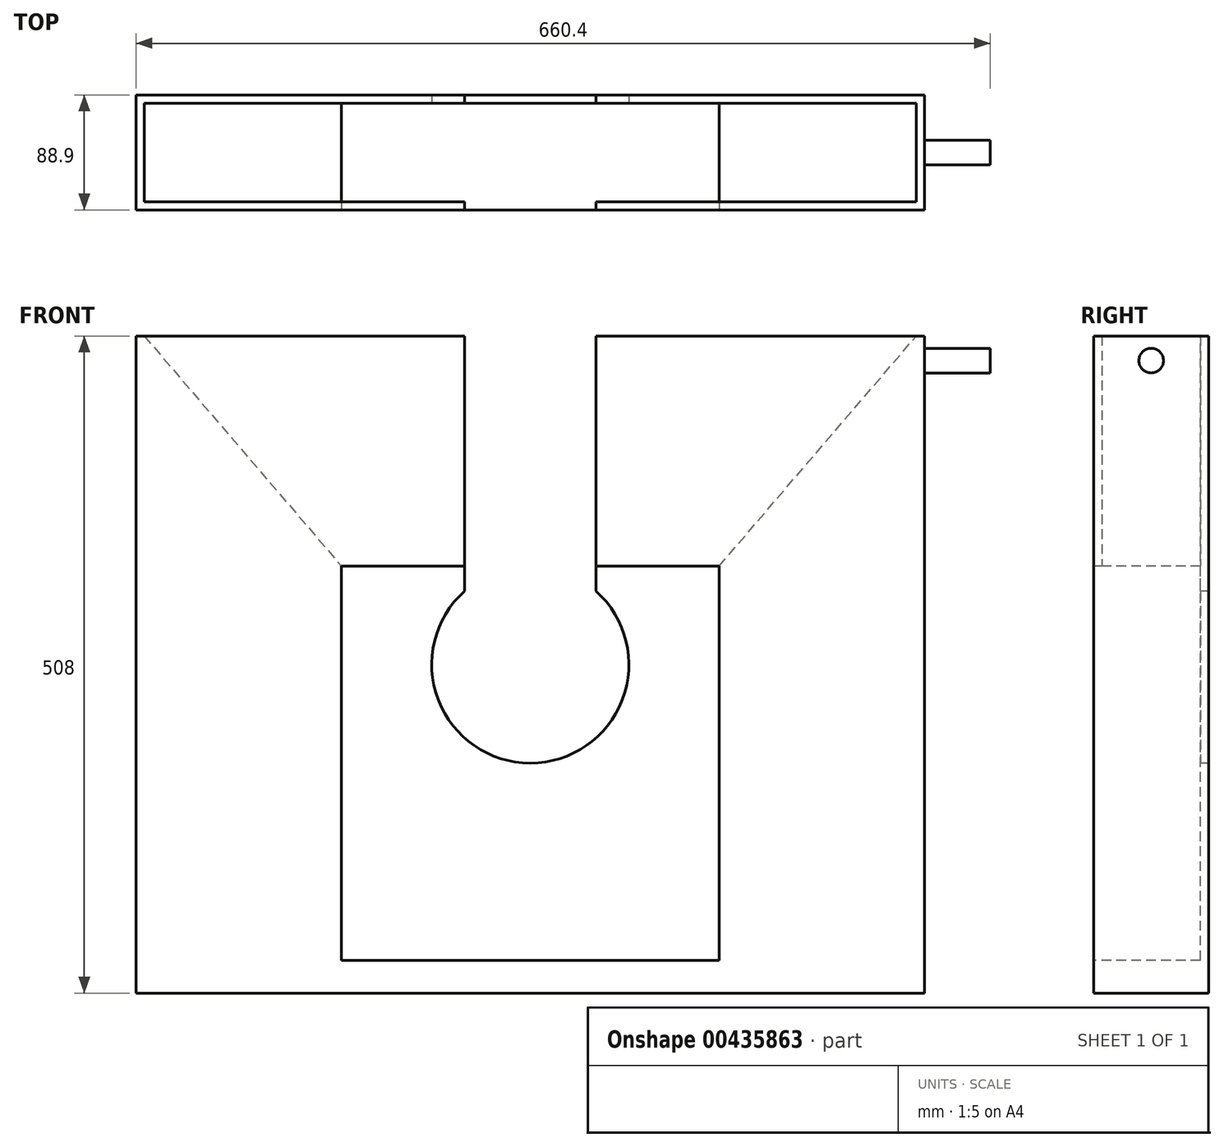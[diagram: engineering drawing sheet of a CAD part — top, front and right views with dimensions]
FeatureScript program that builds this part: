
annotation { "Feature Type Name" : "Feature", "Feature Type Description" : "" }
export const myFeature = defineFeature(function(context is Context, id is Id, definition is map)
    precondition{}
    {
        {
            var Q0;
            Q0=qCreatedBy(makeId("Front.planeOp"),FACE);
            var sketch = newSketch(context, id + "F0", { "sketchPlane" : qUnion([Q0])});
            skLineSegment(sketch, "E0.bottom", {"start": v(-304.8, 254) * mm, "end": v(304.8, 254) * mm});
            skLineSegment(sketch, "E0.top", {"start": v(-304.8, -254) * mm, "end": v(304.8, -254) * mm});
            skLineSegment(sketch, "E0.left", {"start": v(-304.8, 254) * mm, "end": v(-304.8, -254) * mm});
            skLineSegment(sketch, "E0.right", {"start": v(304.8, 254) * mm, "end": v(304.8, -254) * mm});
            skPoint(sketch, "E0.middle", {"position": v(0, 0) * mm});
            skSolve(sketch);
        }
        {
            var Q0;
            Q0=makeQuery(id+"F0.imprint","IMPRINT",FACE,{"disambiguationData":[TD([[makeQuery(id+"F0.imprint","IMPRINT",EDGE,{"derivedFrom":sQuery(id+"F0.wireOp",EDGE,"E0.bottom")}),-1.0]])]});
            extrude(context, id + "F1", {"entities" : qUnion([Q0]), "depth" : 88.9 * mm});
        }
        {
            var Q0;
            Q0=makeQuery(id+"F1.opExtrude","SWEPT_FACE",FACE,{"disambiguationData":[OSD([sQuery(id+"F0.wireOp",EDGE,"E0.bottom")])]});
            var sketch = newSketch(context, id + "F2", { "sketchPlane" : qUnion([Q0])});
            skLineSegment(sketch, "E1.bottom", {"start": v(-298.45, -6.35) * mm, "end": v(298.45, -6.35) * mm});
            skLineSegment(sketch, "E1.top", {"start": v(-298.45, -88.9) * mm, "end": v(298.45, -88.9) * mm});
            skLineSegment(sketch, "E1.left", {"start": v(-298.45, -6.35) * mm, "end": v(-298.45, -88.9) * mm});
            skLineSegment(sketch, "E1.right", {"start": v(298.45, -6.35) * mm, "end": v(298.45, -88.9) * mm});
            skSolve(sketch);
        }
        {
            var Q0;
            Q0=makeQuery(id+"F2.imprint","IMPRINT",FACE,{"disambiguationData":[TD([[makeQuery(id+"F2.imprint","IMPRINT",EDGE,{"derivedFrom":sQuery(id+"F2.wireOp",EDGE,"E1.bottom")}),-1.0]])]});
            extrude(context, id + "F3", {"entities" : qUnion([Q0]), "operationType" : NewBodyOperationType.REMOVE, "oppositeDirection" : true, "depth" : 482.6 * mm});
        }
        {
            var Q0;
            Q0=makeQuery(id+"F1.opExtrude","SWEPT_FACE",FACE,{"disambiguationData":[OSD([sQuery(id+"F0.wireOp",EDGE,"E0.right")])]});
            var sketch = newSketch(context, id + "F4", { "sketchPlane" : qUnion([Q0])});
            skCircle(sketch, "E2", {"center": v(-44.45, 234.95) * mm, "radius": 9.53 * mm});
            skSolve(sketch);
        }
        {
            var Q0;
            Q0=makeQuery(id+"F4.imprint","IMPRINT",FACE,{"disambiguationData":[TD([[makeQuery(id+"F4.imprint","IMPRINT",EDGE,{"derivedFrom":sQuery(id+"F4.wireOp",EDGE,"E2")}),1.0]])]});
            extrude(context, id + "F5", {"entities" : qUnion([Q0]), "operationType" : NewBodyOperationType.ADD, "depth" : 50.8 * mm});
        }
        {
            var Q0;
            Q0=makeQuery(id+"F1.opExtrude","CAP_FACE",FACE,{"disambiguationData":[OSD([sQuery(id+"F0.wireOp",EDGE,"E0.bottom"),sQuery(id+"F0.wireOp",EDGE,"E0.top"),sQuery(id+"F0.wireOp",EDGE,"E0.left"),sQuery(id+"F0.wireOp",EDGE,"E0.right")])],"isStart":false});
            var sketch = newSketch(context, id + "F6", { "sketchPlane" : qUnion([Q0])});
            skLineSegment(sketch, "E3", {"start": v(-298.45, -228.6) * mm, "end": v(-298.45, 76.2) * mm});
            skLineSegment(sketch, "E4", {"start": v(-298.45, 76.2) * mm, "end": v(-146.05, 76.2) * mm});
            skLineSegment(sketch, "E5", {"start": v(-146.05, 76.2) * mm, "end": v(146.05, 76.2) * mm});
            skLineSegment(sketch, "E6", {"start": v(146.05, 76.2) * mm, "end": v(298.45, 76.2) * mm});
            skLineSegment(sketch, "E7", {"start": v(-146.05, 76.2) * mm, "end": v(-298.45, 254) * mm});
            skLineSegment(sketch, "E8", {"start": v(-298.45, 254) * mm, "end": v(-298.45, 76.2) * mm});
            skLineSegment(sketch, "E9", {"start": v(146.05, 76.2) * mm, "end": v(298.45, 254) * mm});
            skLineSegment(sketch, "E10", {"start": v(298.45, 254) * mm, "end": v(298.45, 76.2) * mm});
            skSolve(sketch);
        }
        {
            var Q0;
            Q0=makeQuery(id+"F6.imprint","IMPRINT",FACE,{"disambiguationData":[TD([[makeQuery(id+"F6.imprint","IMPRINT",EDGE,{"derivedFrom":sQuery(id+"F6.wireOp",EDGE,"E4")}),1.0]])]});
            var Q1;
            Q1=makeQuery(id+"F6.imprint","IMPRINT",FACE,{"disambiguationData":[TD([[makeQuery(id+"F6.imprint","IMPRINT",EDGE,{"derivedFrom":sQuery(id+"F6.wireOp",EDGE,"E6")}),1.0]])]});
            var Q2;
            Q2=makeQuery(id+"F3.boolean.opBoolean","COPY",FACE,{"derivedFrom":makeQuery(id+"F3.opExtrude","SWEPT_FACE",FACE,{"disambiguationData":[OSD([sQuery(id+"F2.wireOp",EDGE,"E1.bottom")])]})});
            extrude(context, id + "F7", {"entities" : qUnion([Q0, Q1]), "operationType" : NewBodyOperationType.ADD, "endBound" : BoundingType.UP_TO_SURFACE, "oppositeDirection" : true, "endBoundEntityFace" : qUnion([Q2]), "depth" : 25.4 * mm});
        }
        {
            var Q0;
            Q0=makeQuery(id+"F7.boolean.opBoolean","MERGE",FACE,{"derivedFrom":[makeQuery(id+"F1.opExtrude","CAP_FACE",FACE,{"disambiguationData":[OSD([sQuery(id+"F0.wireOp",EDGE,"E0.bottom"),sQuery(id+"F0.wireOp",EDGE,"E0.top"),sQuery(id+"F0.wireOp",EDGE,"E0.left"),sQuery(id+"F0.wireOp",EDGE,"E0.right")])],"isStart":false}),makeQuery(id+"F7.opExtrude","CAP_FACE",FACE,{"disambiguationData":[OSD([sQuery(id+"F6.wireOp",EDGE,"E4"),sQuery(id+"F6.wireOp",EDGE,"E7"),sQuery(id+"F6.wireOp",EDGE,"E8")])],"isStart":true}),makeQuery(id+"F7.opExtrude","CAP_FACE",FACE,{"disambiguationData":[OSD([sQuery(id+"F6.wireOp",EDGE,"E6"),sQuery(id+"F6.wireOp",EDGE,"E9"),sQuery(id+"F6.wireOp",EDGE,"E10")])],"isStart":true})]});
            var sketch = newSketch(context, id + "F8", { "sketchPlane" : qUnion([Q0])});
            skLineSegment(sketch, "E11.bottom", {"start": v(-146.05, 76.2) * mm, "end": v(-298.45, 76.2) * mm});
            skLineSegment(sketch, "E11.top", {"start": v(-146.05, -228.6) * mm, "end": v(-298.45, -228.6) * mm});
            skLineSegment(sketch, "E11.left", {"start": v(-146.05, 76.2) * mm, "end": v(-146.05, -228.6) * mm});
            skLineSegment(sketch, "E11.right", {"start": v(-298.45, 76.2) * mm, "end": v(-298.45, -228.6) * mm});
            skLineSegment(sketch, "E12.bottom", {"start": v(146.05, 76.2) * mm, "end": v(298.45, 76.2) * mm});
            skLineSegment(sketch, "E12.top", {"start": v(146.05, -228.6) * mm, "end": v(298.45, -228.6) * mm});
            skLineSegment(sketch, "E12.left", {"start": v(146.05, 76.2) * mm, "end": v(146.05, -228.6) * mm});
            skLineSegment(sketch, "E12.right", {"start": v(298.45, 76.2) * mm, "end": v(298.45, -228.6) * mm});
            skSolve(sketch);
        }
        {
            var Q0;
            Q0=makeQuery(id+"F8.imprint","IMPRINT",FACE,{"disambiguationData":[TD([[makeQuery(id+"F8.imprint","IMPRINT",EDGE,{"derivedFrom":sQuery(id+"F8.wireOp",EDGE,"E11.bottom")}),-1.0]])]});
            var Q1;
            Q1=makeQuery(id+"F8.imprint","IMPRINT",FACE,{"disambiguationData":[TD([[makeQuery(id+"F8.imprint","IMPRINT",EDGE,{"derivedFrom":sQuery(id+"F8.wireOp",EDGE,"E12.bottom")}),-1.0]])]});
            var Q2;
            Q2=makeQuery(id+"F3.boolean.opBoolean","COPY",FACE,{"derivedFrom":makeQuery(id+"F3.opExtrude","SWEPT_FACE",FACE,{"disambiguationData":[OSD([sQuery(id+"F2.wireOp",EDGE,"E1.bottom")])]})});
            extrude(context, id + "F9", {"entities" : qUnion([Q0, Q1]), "operationType" : NewBodyOperationType.ADD, "endBound" : BoundingType.UP_TO_SURFACE, "oppositeDirection" : true, "endBoundEntityFace" : qUnion([Q2]), "depth" : 25.4 * mm});
        }
        {
            var Q0;
            Q0=makeQuery(id+"F9.boolean.opBoolean","MERGE",FACE,{"derivedFrom":[makeQuery(id+"F7.boolean.opBoolean","MERGE",FACE,{"derivedFrom":[makeQuery(id+"F1.opExtrude","CAP_FACE",FACE,{"disambiguationData":[OSD([sQuery(id+"F0.wireOp",EDGE,"E0.bottom"),sQuery(id+"F0.wireOp",EDGE,"E0.top"),sQuery(id+"F0.wireOp",EDGE,"E0.left"),sQuery(id+"F0.wireOp",EDGE,"E0.right")])],"isStart":false}),makeQuery(id+"F7.opExtrude","CAP_FACE",FACE,{"disambiguationData":[OSD([sQuery(id+"F6.wireOp",EDGE,"E4"),sQuery(id+"F6.wireOp",EDGE,"E7"),sQuery(id+"F6.wireOp",EDGE,"E8")])],"isStart":true}),makeQuery(id+"F7.opExtrude","CAP_FACE",FACE,{"disambiguationData":[OSD([sQuery(id+"F6.wireOp",EDGE,"E6"),sQuery(id+"F6.wireOp",EDGE,"E9"),sQuery(id+"F6.wireOp",EDGE,"E10")])],"isStart":true})]}),makeQuery(id+"F9.opExtrude","CAP_FACE",FACE,{"disambiguationData":[OSD([sQuery(id+"F8.wireOp",EDGE,"E11.bottom"),sQuery(id+"F8.wireOp",EDGE,"E11.top"),sQuery(id+"F8.wireOp",EDGE,"E11.left"),sQuery(id+"F8.wireOp",EDGE,"E11.right")])],"isStart":true}),makeQuery(id+"F9.opExtrude","CAP_FACE",FACE,{"disambiguationData":[OSD([sQuery(id+"F8.wireOp",EDGE,"E12.bottom"),sQuery(id+"F8.wireOp",EDGE,"E12.top"),sQuery(id+"F8.wireOp",EDGE,"E12.left"),sQuery(id+"F8.wireOp",EDGE,"E12.right")])],"isStart":true})]});
            var sketch = newSketch(context, id + "F10", { "sketchPlane" : qUnion([Q0])});
            skLineSegment(sketch, "E13", {"start": v(-298.45, 254) * mm, "end": v(298.45, 254) * mm});
            skLineSegment(sketch, "E14", {"start": v(298.45, 254) * mm, "end": v(146.05, 76.2) * mm});
            skLineSegment(sketch, "E15", {"start": v(146.05, 76.2) * mm, "end": v(-146.05, 76.2) * mm});
            skLineSegment(sketch, "E16", {"start": v(-146.05, 76.2) * mm, "end": v(-298.45, 254) * mm});
            skSolve(sketch);
        }
        {
            var Q0;
            Q0=makeQuery(id+"F10.imprint","IMPRINT",FACE,{"disambiguationData":[TD([[makeQuery(id+"F10.imprint","IMPRINT",EDGE,{"derivedFrom":sQuery(id+"F10.wireOp",EDGE,"E13")}),-1.0]])]});
            extrude(context, id + "F11", {"entities" : qUnion([Q0]), "operationType" : NewBodyOperationType.ADD, "oppositeDirection" : true, "depth" : 6.35 * mm});
        }
        {
            var Q0;
            Q0=makeQuery(id+"F3.boolean.opBoolean","COPY",FACE,{"derivedFrom":makeQuery(id+"F3.opExtrude","SWEPT_FACE",FACE,{"disambiguationData":[OSD([sQuery(id+"F2.wireOp",EDGE,"E1.bottom")])]})});
            var sketch = newSketch(context, id + "F12", { "sketchPlane" : qUnion([Q0])});
            skCircle(sketch, "E17", {"center": v(0, 0) * mm, "radius": 76.2 * mm});
            skLineSegment(sketch, "E18", {"start": v(-146.05, -228.6) * mm, "end": v(146.05, -228.6) * mm});
            skSolve(sketch);
        }
        {
            var Q0;
            Q0=makeQuery(id+"F12.imprint","IMPRINT",FACE,{"disambiguationData":[TD([[makeQuery(id+"F12.imprint","IMPRINT",EDGE,{"derivedFrom":sQuery(id+"F12.wireOp",EDGE,"E17")}),1.0]])]});
            extrude(context, id + "F13", {"entities" : qUnion([Q0]), "operationType" : NewBodyOperationType.REMOVE, "oppositeDirection" : true, "depth" : 25.4 * mm});
        }
        {
            var Q0;
            Q0=makeQuery(id+"F11.boolean.opBoolean","MERGE",FACE,{"derivedFrom":[makeQuery(id+"F9.boolean.opBoolean","MERGE",FACE,{"derivedFrom":[makeQuery(id+"F7.boolean.opBoolean","MERGE",FACE,{"derivedFrom":[makeQuery(id+"F1.opExtrude","CAP_FACE",FACE,{"disambiguationData":[OSD([sQuery(id+"F0.wireOp",EDGE,"E0.bottom"),sQuery(id+"F0.wireOp",EDGE,"E0.top"),sQuery(id+"F0.wireOp",EDGE,"E0.left"),sQuery(id+"F0.wireOp",EDGE,"E0.right")])],"isStart":false}),makeQuery(id+"F7.opExtrude","CAP_FACE",FACE,{"disambiguationData":[OSD([sQuery(id+"F6.wireOp",EDGE,"E4"),sQuery(id+"F6.wireOp",EDGE,"E7"),sQuery(id+"F6.wireOp",EDGE,"E8")])],"isStart":true}),makeQuery(id+"F7.opExtrude","CAP_FACE",FACE,{"disambiguationData":[OSD([sQuery(id+"F6.wireOp",EDGE,"E6"),sQuery(id+"F6.wireOp",EDGE,"E9"),sQuery(id+"F6.wireOp",EDGE,"E10")])],"isStart":true})]}),makeQuery(id+"F9.opExtrude","CAP_FACE",FACE,{"disambiguationData":[OSD([sQuery(id+"F8.wireOp",EDGE,"E11.bottom"),sQuery(id+"F8.wireOp",EDGE,"E11.top"),sQuery(id+"F8.wireOp",EDGE,"E11.left"),sQuery(id+"F8.wireOp",EDGE,"E11.right")])],"isStart":true}),makeQuery(id+"F9.opExtrude","CAP_FACE",FACE,{"disambiguationData":[OSD([sQuery(id+"F8.wireOp",EDGE,"E12.bottom"),sQuery(id+"F8.wireOp",EDGE,"E12.top"),sQuery(id+"F8.wireOp",EDGE,"E12.left"),sQuery(id+"F8.wireOp",EDGE,"E12.right")])],"isStart":true})]}),makeQuery(id+"F11.opExtrude","CAP_FACE",FACE,{"disambiguationData":[OSD([sQuery(id+"F10.wireOp",EDGE,"E13"),sQuery(id+"F10.wireOp",EDGE,"E14"),sQuery(id+"F10.wireOp",EDGE,"E15"),sQuery(id+"F10.wireOp",EDGE,"E16")])],"isStart":true})]});
            var sketch = newSketch(context, id + "F14", { "sketchPlane" : qUnion([Q0])});
            skLineSegment(sketch, "E19.bottom", {"start": v(-50.8, 254) * mm, "end": v(50.8, 254) * mm});
            skLineSegment(sketch, "E19.top", {"start": v(-50.8, 76.2) * mm, "end": v(50.8, 76.2) * mm});
            skLineSegment(sketch, "E19.left", {"start": v(-50.8, 254) * mm, "end": v(-50.8, 76.2) * mm});
            skLineSegment(sketch, "E19.right", {"start": v(50.8, 254) * mm, "end": v(50.8, 76.2) * mm});
            skLineSegment(sketch, "E20", {"start": v(-304.8, 254) * mm, "end": v(304.8, 254) * mm});
            skSolve(sketch);
        }
        {
            var Q0;
            Q0=makeQuery(id+"F14.imprint","IMPRINT",FACE,{"disambiguationData":[TD([[makeQuery(id+"F14.imprint","IMPRINT",EDGE,{"derivedFrom":sQuery(id+"F14.wireOp",EDGE,"E19.top")}),-1.0]])]});
            extrude(context, id + "F15", {"entities" : qUnion([Q0]), "operationType" : NewBodyOperationType.REMOVE, "oppositeDirection" : true, "depth" : 25.4 * mm});
        }
        {
            var Q0;
            Q0=makeQuery(id+"F0.imprint","IMPRINT",FACE,{"disambiguationData":[TD([[makeQuery(id+"F0.imprint","IMPRINT",EDGE,{"derivedFrom":sQuery(id+"F0.wireOp",EDGE,"E0.bottom")}),-1.0]])]});
            var sketch = newSketch(context, id + "F16", { "sketchPlane" : qUnion([Q0])});
            skLineSegment(sketch, "E21.bottom", {"start": v(50.8, 254) * mm, "end": v(-50.8, 254) * mm});
            skLineSegment(sketch, "E21.top", {"start": v(50.8, 54.6) * mm, "end": v(-50.8, 54.6) * mm});
            skLineSegment(sketch, "E21.left", {"start": v(50.8, 254) * mm, "end": v(50.8, 54.6) * mm});
            skLineSegment(sketch, "E21.right", {"start": v(-50.8, 254) * mm, "end": v(-50.8, 54.6) * mm});
            skSolve(sketch);
        }
        {
            var Q0;
            Q0=makeQuery(id+"F16.imprint","IMPRINT",FACE,{"disambiguationData":[TD([[makeQuery(id+"F16.imprint","IMPRINT",EDGE,{"derivedFrom":sQuery(id+"F16.wireOp",EDGE,"E21.bottom")}),-1.0]])]});
            extrude(context, id + "F17", {"entities" : qUnion([Q0]), "operationType" : NewBodyOperationType.REMOVE, "depth" : 25.4 * mm});
        }
    });
